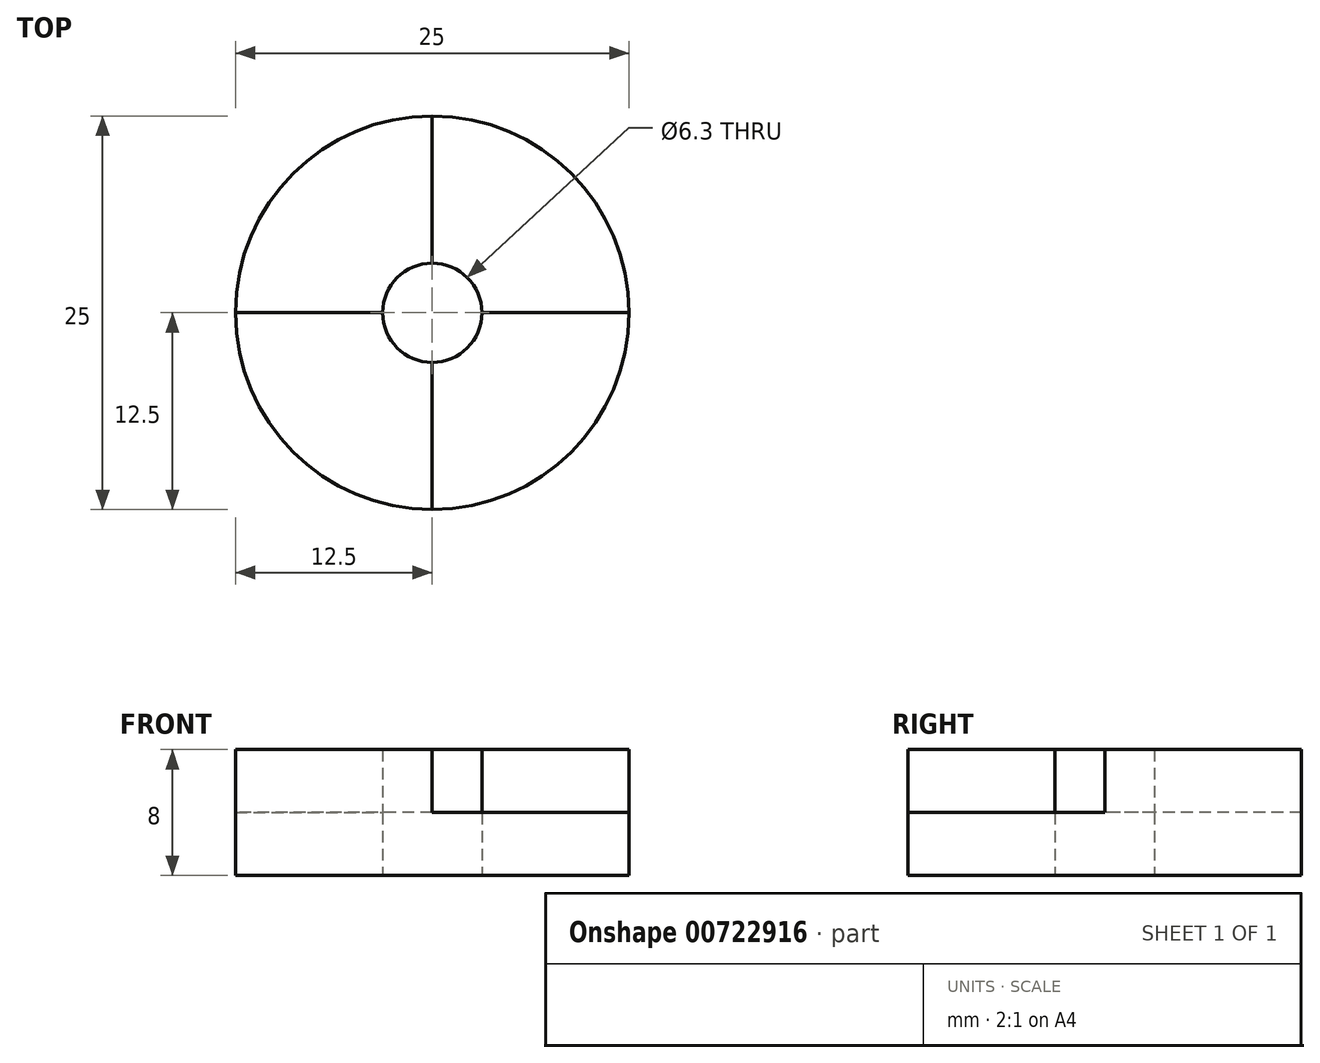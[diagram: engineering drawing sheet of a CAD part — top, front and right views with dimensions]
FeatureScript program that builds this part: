
annotation { "Feature Type Name" : "Feature", "Feature Type Description" : "" }
export const myFeature = defineFeature(function(context is Context, id is Id, definition is map)
    precondition{}
    {
        {
            var Q0;
            Q0=qCreatedBy(makeId("Top.planeOp"),FACE);
            var sketch = newSketch(context, id + "F0", { "sketchPlane" : qUnion([Q0])});
            skCircle(sketch, "E0", {"center": v(0, 0) * mm, "radius": 12.5 * mm});
            skCircle(sketch, "E1", {"center": v(0, 0) * mm, "radius": 3.15 * mm});
            skLineSegment(sketch, "E2", {"start": v(0, 3.15) * mm, "end": v(0, 12.5) * mm});
            skLineSegment(sketch, "E3", {"start": v(-3.15, 0) * mm, "end": v(-12.5, 0) * mm});
            skLineSegment(sketch, "E4", {"start": v(0, -3.15) * mm, "end": v(0, -12.5) * mm});
            skLineSegment(sketch, "E5", {"start": v(3.15, 0) * mm, "end": v(12.5, 0) * mm});
            skSolve(sketch);
        }
        {
            var Q0;
            {var subQ0=sQuery(id+"F0.wireOp",EDGE,"E3");Q0=makeQuery(id+"F0.imprint","IMPRINT",FACE,{"disambiguationData":[TD([[makeQuery(id+"F0.imprint","IMPRINT",EDGE,{"derivedFrom":subQ0}),1.0]])]});}
            var Q1;
            {var subQ0=sQuery(id+"F0.wireOp",EDGE,"E2");Q1=makeQuery(id+"F0.imprint","IMPRINT",FACE,{"disambiguationData":[TD([[makeQuery(id+"F0.imprint","IMPRINT",EDGE,{"derivedFrom":subQ0}),1.0]])]});}
            var Q2;
            {var subQ0=sQuery(id+"F0.wireOp",EDGE,"E2");Q2=makeQuery(id+"F0.imprint","IMPRINT",FACE,{"disambiguationData":[TD([[makeQuery(id+"F0.imprint","IMPRINT",EDGE,{"derivedFrom":subQ0}),-1.0]])]});}
            var Q3;
            {var subQ0=sQuery(id+"F0.wireOp",EDGE,"E4");Q3=makeQuery(id+"F0.imprint","IMPRINT",FACE,{"disambiguationData":[TD([[makeQuery(id+"F0.imprint","IMPRINT",EDGE,{"derivedFrom":subQ0}),1.0]])]});}
            extrude(context, id + "F1", {"entities" : qUnion([Q0, Q1, Q2, Q3]), "depth" : 4 * mm, "offsetDistance" : 25 * mm});
        }
        {
            var Q0;
            {var subQ0=sQuery(id+"F0.wireOp",EDGE,"E2");Q0=makeQuery(id+"F0.imprint","IMPRINT",FACE,{"disambiguationData":[TD([[makeQuery(id+"F0.imprint","IMPRINT",EDGE,{"derivedFrom":subQ0}),-1.0]])]});}
            var Q1;
            {var subQ0=sQuery(id+"F0.wireOp",EDGE,"E3");Q1=makeQuery(id+"F0.imprint","IMPRINT",FACE,{"disambiguationData":[TD([[makeQuery(id+"F0.imprint","IMPRINT",EDGE,{"derivedFrom":subQ0}),1.0]])]});}
            extrude(context, id + "F2", {"entities" : qUnion([Q0, Q1]), "operationType" : NewBodyOperationType.ADD, "depth" : 8 * mm, "offsetDistance" : 25 * mm});
        }
    });
